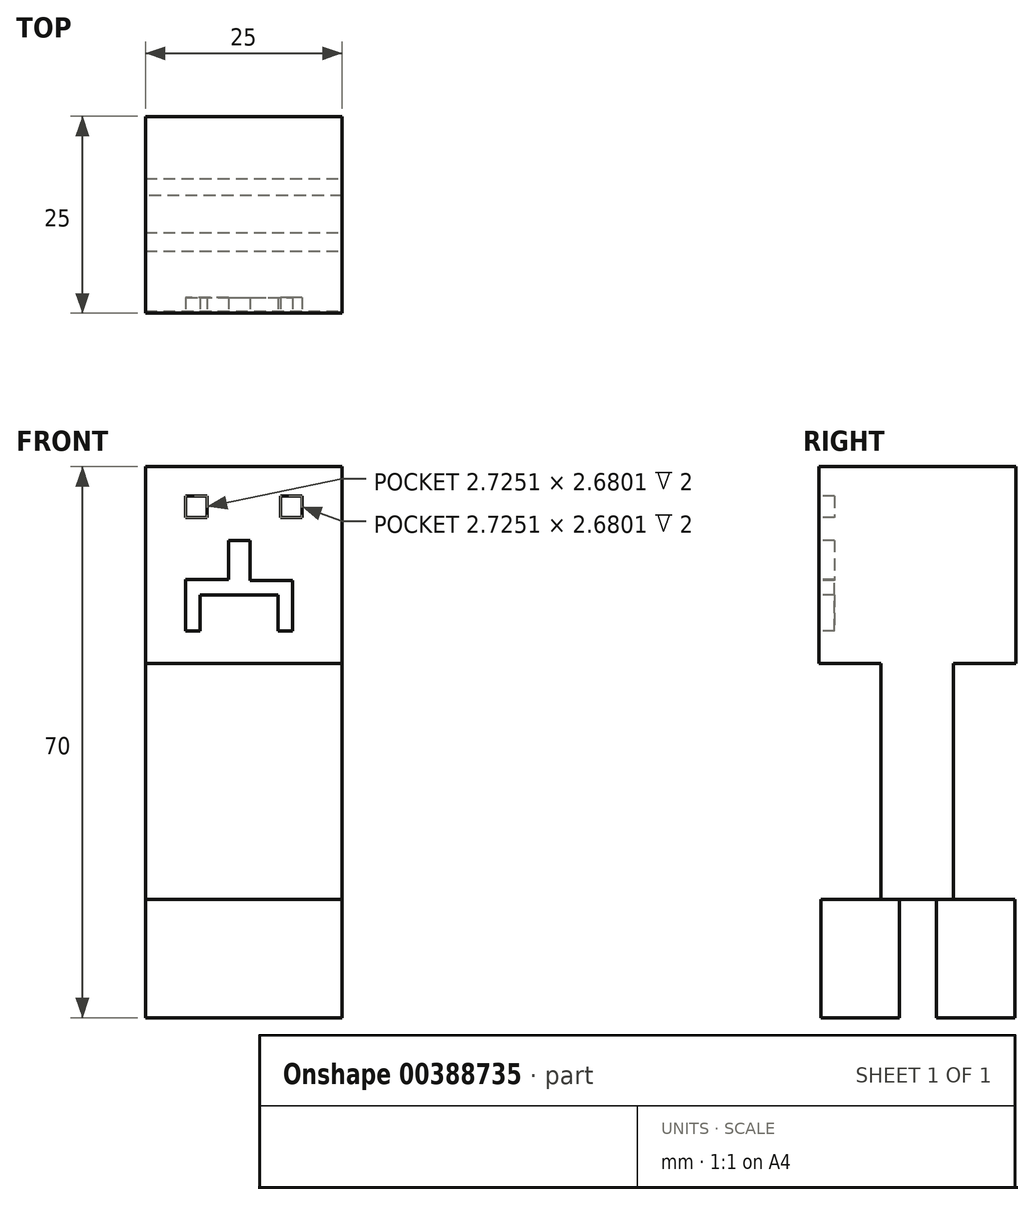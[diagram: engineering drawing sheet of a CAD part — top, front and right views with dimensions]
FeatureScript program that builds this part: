
annotation { "Feature Type Name" : "Feature", "Feature Type Description" : "" }
export const myFeature = defineFeature(function(context is Context, id is Id, definition is map)
    precondition{}
    {
        {
            var Q0;
            Q0=qCreatedBy(makeId("Top.planeOp"),FACE);
            var sketch = newSketch(context, id + "F0", { "sketchPlane" : qUnion([Q0])});
            skLineSegment(sketch, "E0.bottom", {"start": v(6.33, 14.68) * mm, "end": v(-18.67, 14.68) * mm});
            skLineSegment(sketch, "E0.top", {"start": v(6.33, 24.68) * mm, "end": v(-18.67, 24.68) * mm});
            skLineSegment(sketch, "E0.left", {"start": v(6.33, 14.68) * mm, "end": v(6.33, 24.68) * mm});
            skLineSegment(sketch, "E0.right", {"start": v(-18.67, 14.68) * mm, "end": v(-18.67, 24.68) * mm});
            skPoint(sketch, "E0.middle", {"position": v(-6.17, 19.68) * mm});
            skLineSegment(sketch, "E1.bottom", {"start": v(-18.67, 0) * mm, "end": v(6.33, 0) * mm});
            skLineSegment(sketch, "E1.top", {"start": v(-18.67, 10) * mm, "end": v(6.33, 10) * mm});
            skLineSegment(sketch, "E1.left", {"start": v(-18.67, 0) * mm, "end": v(-18.67, 10) * mm});
            skLineSegment(sketch, "E1.right", {"start": v(6.33, 0) * mm, "end": v(6.33, 10) * mm});
            skPoint(sketch, "E1.middle", {"position": v(-6.17, 5) * mm});
            skSolve(sketch);
        }
        {
            var Q0;
            Q0=makeQuery(id+"F0.imprint","IMPRINT",FACE,{"disambiguationData":[TD([[makeQuery(id+"F0.imprint","IMPRINT",EDGE,{"derivedFrom":sQuery(id+"F0.wireOp",EDGE,"E0.bottom")}),-1.0]])]});
            var Q1;
            Q1=makeQuery(id+"F0.imprint","IMPRINT",FACE,{"disambiguationData":[TD([[makeQuery(id+"F0.imprint","IMPRINT",EDGE,{"derivedFrom":sQuery(id+"F0.wireOp",EDGE,"E1.bottom")}),1.0]])]});
            extrude(context, id + "F1", {"entities" : qUnion([Q0, Q1]), "depth" : 15 * mm});
        }
        {
            var Q0;
            Q0=makeQuery(id+"F1.opExtrude","CAP_FACE",FACE,{"disambiguationData":[OSD([sQuery(id+"F0.wireOp",EDGE,"E0.bottom"),sQuery(id+"F0.wireOp",EDGE,"E0.top"),sQuery(id+"F0.wireOp",EDGE,"E0.left"),sQuery(id+"F0.wireOp",EDGE,"E0.right")])],"isStart":false});
            var sketch = newSketch(context, id + "F2", { "sketchPlane" : qUnion([Q0])});
            skLineSegment(sketch, "E2.bottom", {"start": v(-18.67, 16.86) * mm, "end": v(6.33, 16.86) * mm});
            skLineSegment(sketch, "E2.top", {"start": v(-18.67, 7.66) * mm, "end": v(6.33, 7.66) * mm});
            skLineSegment(sketch, "E2.left", {"start": v(-18.67, 16.86) * mm, "end": v(-18.67, 7.66) * mm});
            skLineSegment(sketch, "E2.right", {"start": v(6.33, 16.86) * mm, "end": v(6.33, 7.66) * mm});
            skPoint(sketch, "E2.middle", {"position": v(-6.17, 12.26) * mm});
            skSolve(sketch);
        }
        {
            var Q0;
            {var subQ0=sQuery(id+"F2.wireOp",EDGE,"E2.top");Q0=makeQuery(id+"F2.imprint","IMPRINT",FACE,{"disambiguationData":[TD([[makeQuery(id+"F2.imprint","IMPRINT",EDGE,{"derivedFrom":subQ0}),1.0]])]});}
            var Q1;
            {var subQ0=sQuery(id+"F2.wireOp",EDGE,"E2.bottom");Q1=makeQuery(id+"F2.imprint","IMPRINT",FACE,{"disambiguationData":[TD([[makeQuery(id+"F2.imprint","IMPRINT",EDGE,{"derivedFrom":subQ0}),-1.0]])]});}
            extrude(context, id + "F3", {"entities" : qUnion([Q0, Q1]), "depth" : 30 * mm});
        }
        {
            var Q0;
            Q0=makeQuery(id+"F3.opExtrude","CAP_FACE",FACE,{"disambiguationData":[OSD([sQuery(id+"F2.wireOp",EDGE,"E2.bottom"),sQuery(id+"F2.wireOp",EDGE,"E2.top"),sQuery(id+"F2.wireOp",EDGE,"E2.left"),sQuery(id+"F2.wireOp",EDGE,"E2.right")])],"isStart":false});
            var sketch = newSketch(context, id + "F4", { "sketchPlane" : qUnion([Q0])});
            skLineSegment(sketch, "E3.bottom", {"start": v(-18.67, 24.76) * mm, "end": v(6.33, 24.76) * mm});
            skLineSegment(sketch, "E3.top", {"start": v(-18.67, -0.24) * mm, "end": v(6.33, -0.24) * mm});
            skLineSegment(sketch, "E3.left", {"start": v(-18.67, 24.76) * mm, "end": v(-18.67, -0.24) * mm});
            skLineSegment(sketch, "E3.right", {"start": v(6.33, 24.76) * mm, "end": v(6.33, -0.24) * mm});
            skPoint(sketch, "E3.middle", {"position": v(-6.17, 12.26) * mm});
            skPoint(sketch, "E3.middle.positionSnap0", {"position": v(6.33, 12.26) * mm});
            skPoint(sketch, "E3.middle.positionSnap1", {"position": v(-6.17, 16.86) * mm});
            skPoint(sketch, "E3.centerSnap0", {"position": v(6.33, 12.26) * mm});
            skPoint(sketch, "E3.centerSnap1", {"position": v(-6.17, 16.86) * mm});
            skSolve(sketch);
        }
        {
            var Q0;
            {var subQ0=sQuery(id+"F4.wireOp",EDGE,"E3.top");Q0=makeQuery(id+"F4.imprint","IMPRINT",FACE,{"disambiguationData":[TD([[makeQuery(id+"F4.imprint","IMPRINT",EDGE,{"derivedFrom":subQ0}),1.0]])]});}
            var Q1;
            {var subQ1=makeQuery(id+"F3.opExtrude","CAP_EDGE",EDGE,{"disambiguationData":[OSD([sQuery(id+"F2.wireOp",EDGE,"E2.bottom")])],"isStart":false});Q1=makeQuery(id+"F4.imprint","IMPRINT",FACE,{"disambiguationData":[TD([[makeQuery(id+"F4.imprint","IMPRINT",EDGE,{"derivedFrom":subQ1}),-1.0]])]});}
            var Q2;
            {var subQ0=sQuery(id+"F4.wireOp",EDGE,"E3.bottom");Q2=makeQuery(id+"F4.imprint","IMPRINT",FACE,{"disambiguationData":[TD([[makeQuery(id+"F4.imprint","IMPRINT",EDGE,{"derivedFrom":subQ0}),-1.0]])]});}
            extrude(context, id + "F5", {"entities" : qUnion([Q0, Q1, Q2]), "operationType" : NewBodyOperationType.ADD, "depth" : 25 * mm});
        }
        {
            var Q0;
            Q0=makeQuery(id+"F5.opExtrude","SWEPT_FACE",FACE,{"disambiguationData":[OSD([sQuery(id+"F4.wireOp",EDGE,"E3.top")])]});
            var sketch = newSketch(context, id + "F6", { "sketchPlane" : qUnion([Q0])});
            skLineSegment(sketch, "E4.bottom", {"start": v(-8.12, 60.63) * mm, "end": v(-5.36, 60.63) * mm});
            skLineSegment(sketch, "E4.top", {"start": v(-8.12, 53.7) * mm, "end": v(-5.36, 53.7) * mm});
            skLineSegment(sketch, "E4.left", {"start": v(-8.12, 60.63) * mm, "end": v(-8.12, 53.7) * mm});
            skLineSegment(sketch, "E4.right", {"start": v(-5.36, 60.63) * mm, "end": v(-5.36, 53.7) * mm});
            skPoint(sketch, "E4.middle", {"position": v(-6.74, 57.16) * mm});
            skLineSegment(sketch, "E5.bottom", {"start": v(-8.12, 53.7) * mm, "end": v(-13.55, 53.7) * mm});
            skLineSegment(sketch, "E5.top", {"start": v(-8.12, 55.64) * mm, "end": v(-13.55, 55.64) * mm});
            skLineSegment(sketch, "E5.left", {"start": v(-8.12, 53.7) * mm, "end": v(-8.12, 55.64) * mm});
            skLineSegment(sketch, "E5.right", {"start": v(-13.55, 53.7) * mm, "end": v(-13.55, 55.64) * mm});
            skLineSegment(sketch, "E6.bottom", {"start": v(-5.36, 53.7) * mm, "end": v(0, 53.7) * mm});
            skLineSegment(sketch, "E6.top", {"start": v(-5.36, 55.55) * mm, "end": v(0, 55.55) * mm});
            skLineSegment(sketch, "E6.left", {"start": v(-5.36, 53.7) * mm, "end": v(-5.36, 55.55) * mm});
            skLineSegment(sketch, "E6.right", {"start": v(0, 53.7) * mm, "end": v(0, 55.55) * mm});
            skLineSegment(sketch, "E7.bottom", {"start": v(-13.55, 55.64) * mm, "end": v(-11.71, 55.64) * mm});
            skLineSegment(sketch, "E7.top", {"start": v(-13.55, 49.12) * mm, "end": v(-11.71, 49.12) * mm});
            skLineSegment(sketch, "E7.left", {"start": v(-13.55, 55.64) * mm, "end": v(-13.55, 49.12) * mm});
            skLineSegment(sketch, "E7.right", {"start": v(-11.71, 55.64) * mm, "end": v(-11.71, 49.12) * mm});
            skLineSegment(sketch, "E8.bottom", {"start": v(0, 55.55) * mm, "end": v(-1.8, 55.55) * mm});
            skLineSegment(sketch, "E8.top", {"start": v(0, 49.12) * mm, "end": v(-1.8, 49.12) * mm});
            skLineSegment(sketch, "E8.left", {"start": v(0, 55.55) * mm, "end": v(0, 49.12) * mm});
            skLineSegment(sketch, "E8.right", {"start": v(-1.8, 55.55) * mm, "end": v(-1.8, 49.12) * mm});
            skLineSegment(sketch, "E9.bottom", {"start": v(-13.55, 66.25) * mm, "end": v(-10.82, 66.25) * mm});
            skLineSegment(sketch, "E9.top", {"start": v(-13.55, 63.57) * mm, "end": v(-10.82, 63.57) * mm});
            skLineSegment(sketch, "E9.left", {"start": v(-13.55, 66.25) * mm, "end": v(-13.55, 63.57) * mm});
            skLineSegment(sketch, "E9.right", {"start": v(-10.82, 66.25) * mm, "end": v(-10.82, 63.57) * mm});
            skLineSegment(sketch, "E10", {"start": v(-6.17, 70) * mm, "end": v(-6.17, 62.28) * mm, "construction": true});
            skLineSegment(sketch, "E11.MirrorCS", {"start": v(1.2, 66.25) * mm, "end": v(-1.53, 66.25) * mm});
            skLineSegment(sketch, "E12.MirrorCS", {"start": v(-1.53, 66.25) * mm, "end": v(-1.53, 63.57) * mm});
            skLineSegment(sketch, "E13.MirrorCS", {"start": v(1.2, 63.57) * mm, "end": v(-1.53, 63.57) * mm});
            skLineSegment(sketch, "E14.MirrorCS", {"start": v(1.2, 66.25) * mm, "end": v(1.2, 63.57) * mm});
            skSolve(sketch);
        }
        {
            var Q0;
            Q0=makeQuery(id+"F6.imprint","IMPRINT",FACE,{"disambiguationData":[TD([[makeQuery(id+"F6.imprint","IMPRINT",EDGE,{"derivedFrom":sQuery(id+"F6.wireOp",EDGE,"E9.bottom")}),-1.0]])]});
            var Q1;
            Q1=makeQuery(id+"F6.imprint","IMPRINT",FACE,{"disambiguationData":[TD([[makeQuery(id+"F6.imprint","IMPRINT",EDGE,{"derivedFrom":sQuery(id+"F6.wireOp",EDGE,"E11.MirrorCS")}),1.0]])]});
            var Q2;
            Q2=makeQuery(id+"F6.imprint","IMPRINT",FACE,{"disambiguationData":[TD([[makeQuery(id+"F6.imprint","IMPRINT",EDGE,{"derivedFrom":sQuery(id+"F6.wireOp",EDGE,"E4.bottom")}),-1.0]])]});
            var Q3;
            {var subQ4=sQuery(id+"F6.wireOp",EDGE,"E6.top");Q3=makeQuery(id+"F6.imprint","IMPRINT",FACE,{"disambiguationData":[TD([[makeQuery(id+"F6.imprint","IMPRINT",EDGE,{"derivedFrom":subQ4}),-1.0]])]});}
            var Q4;
            {var subQ5=sQuery(id+"F6.wireOp",EDGE,"E8.bottom");Q4=makeQuery(id+"F6.imprint","IMPRINT",FACE,{"disambiguationData":[TD([[makeQuery(id+"F6.imprint","IMPRINT",EDGE,{"derivedFrom":subQ5}),1.0]])]});}
            var Q5;
            {var subQ5=sQuery(id+"F6.wireOp",EDGE,"E8.top");Q5=makeQuery(id+"F6.imprint","IMPRINT",FACE,{"disambiguationData":[TD([[makeQuery(id+"F6.imprint","IMPRINT",EDGE,{"derivedFrom":subQ5}),-1.0]])]});}
            var Q6;
            {var subQ4=sQuery(id+"F6.wireOp",EDGE,"E5.top");Q6=makeQuery(id+"F6.imprint","IMPRINT",FACE,{"disambiguationData":[TD([[makeQuery(id+"F6.imprint","IMPRINT",EDGE,{"derivedFrom":subQ4}),1.0]])]});}
            var Q7;
            {var subQ5=sQuery(id+"F6.wireOp",EDGE,"E7.bottom");Q7=makeQuery(id+"F6.imprint","IMPRINT",FACE,{"disambiguationData":[TD([[makeQuery(id+"F6.imprint","IMPRINT",EDGE,{"derivedFrom":subQ5}),-1.0]])]});}
            var Q8;
            {var subQ5=sQuery(id+"F6.wireOp",EDGE,"E7.top");Q8=makeQuery(id+"F6.imprint","IMPRINT",FACE,{"disambiguationData":[TD([[makeQuery(id+"F6.imprint","IMPRINT",EDGE,{"derivedFrom":subQ5}),1.0]])]});}
            extrude(context, id + "F7", {"entities" : qUnion([Q0, Q1, Q2, Q3, Q4, Q5, Q6, Q7, Q8]), "operationType" : NewBodyOperationType.REMOVE, "oppositeDirection" : true, "depth" : 2 * mm});
        }
    });
